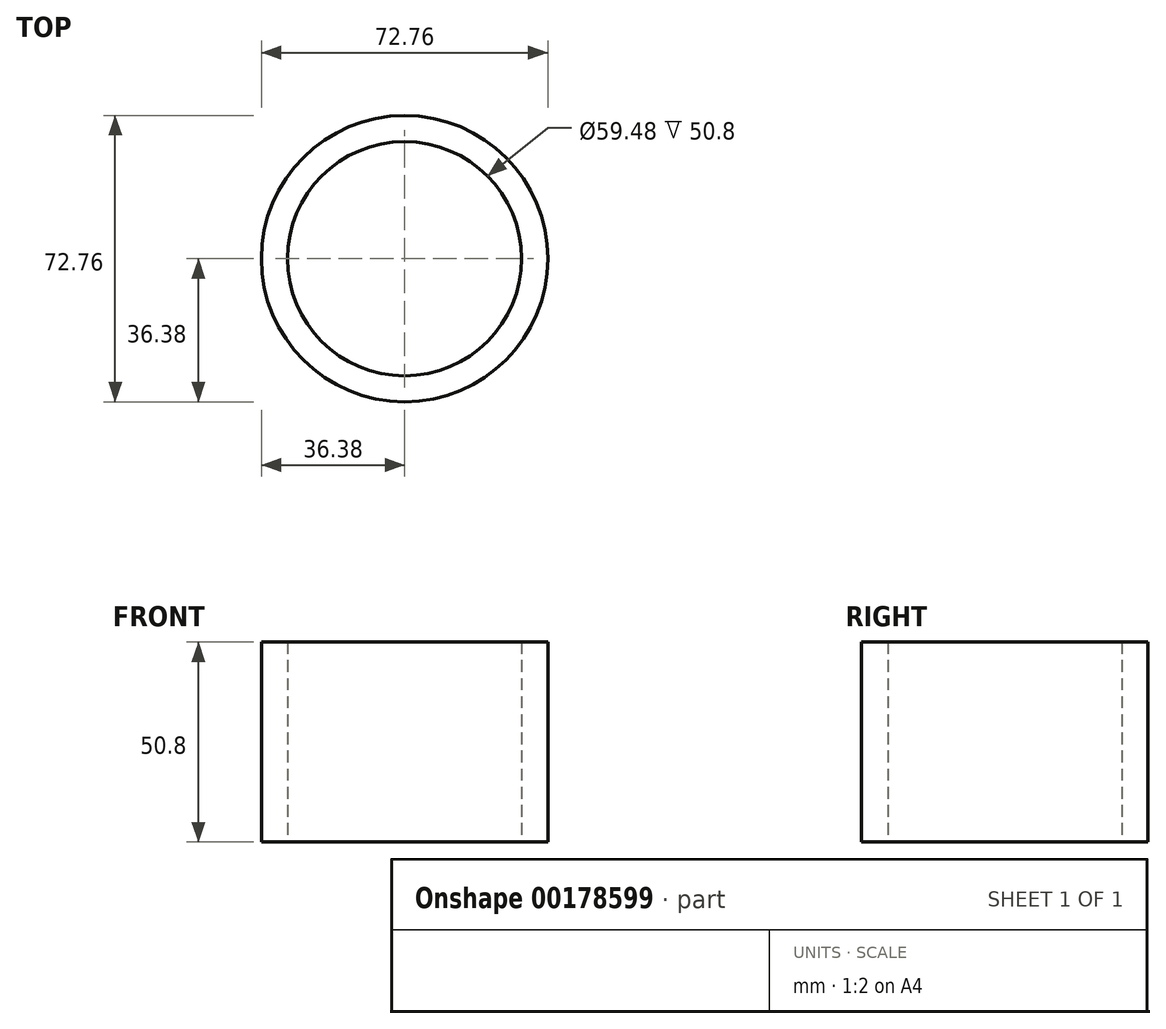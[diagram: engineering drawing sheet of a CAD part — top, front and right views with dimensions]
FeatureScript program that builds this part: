
annotation { "Feature Type Name" : "Feature", "Feature Type Description" : "" }
export const myFeature = defineFeature(function(context is Context, id is Id, definition is map)
    precondition{}
    {
        {
            var Q0;
            Q0=qCreatedBy(makeId("Top.planeOp"),FACE);
            var sketch = newSketch(context, id + "F0", { "sketchPlane" : qUnion([Q0])});
            skCircle(sketch, "E0", {"center": v(0, 0) * mm, "radius": 36.38 * mm});
            skCircle(sketch, "E1", {"center": v(0, 0) * mm, "radius": 29.74 * mm});
            skSolve(sketch);
        }
        {
            var Q0;
            Q0=makeQuery(id+"F0.imprint","IMPRINT",FACE,{"disambiguationData":[TD([[makeQuery(id+"F0.imprint","IMPRINT",EDGE,{"derivedFrom":sQuery(id+"F0.wireOp",EDGE,"E0")}),1.0]])]});
            extrude(context, id + "F1", {"entities" : qUnion([Q0]), "depth" : 50.8 * mm});
        }
    });
